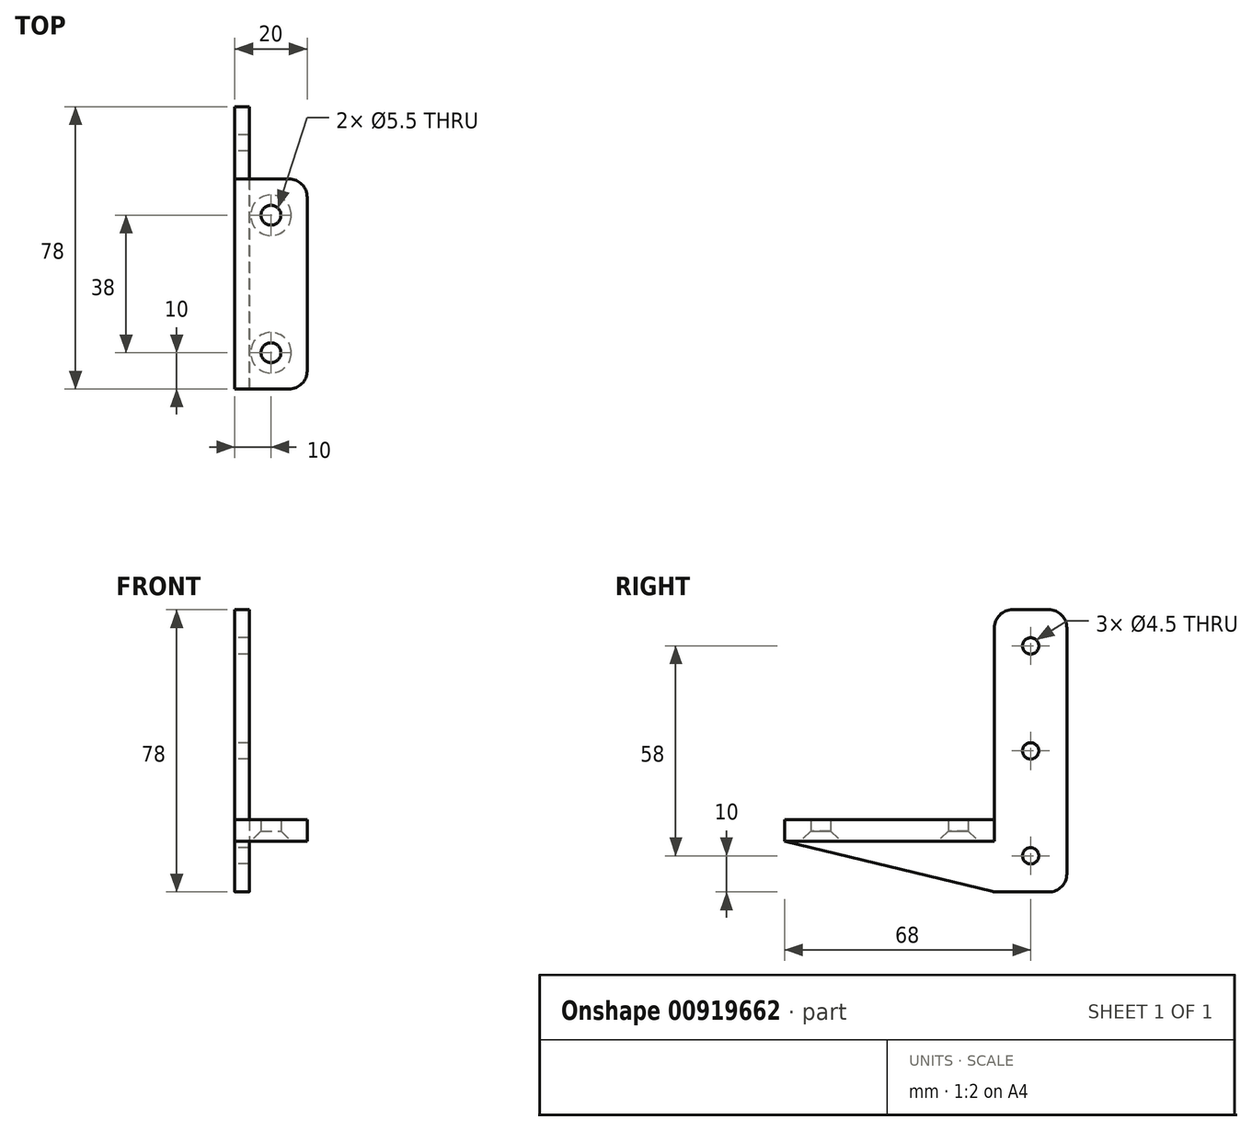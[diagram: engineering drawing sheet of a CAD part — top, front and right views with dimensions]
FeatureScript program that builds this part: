
annotation { "Feature Type Name" : "Feature", "Feature Type Description" : "" }
export const myFeature = defineFeature(function(context is Context, id is Id, definition is map)
    precondition{}
    {
        {
            var Q0;
            Q0=qCreatedBy(makeId("Right.planeOp"),FACE);
            var sketch = newSketch(context, id + "F0", { "sketchPlane" : qUnion([Q0])});
            skLineSegment(sketch, "E0", {"start": v(-29, 0) * mm, "end": v(29, 0) * mm});
            skLineSegment(sketch, "E1", {"start": v(29, -6) * mm, "end": v(-29, -6) * mm});
            skLineSegment(sketch, "E2", {"start": v(-29, 0) * mm, "end": v(-29, -6) * mm});
            skLineSegment(sketch, "E3", {"start": v(29, 0) * mm, "end": v(29, -6) * mm});
            skSolve(sketch);
        }
        {
            var Q0;
            Q0=qCreatedBy(makeId("Right.planeOp"),FACE);
            var sketch = newSketch(context, id + "F1", { "sketchPlane" : qUnion([Q0])});
            skLineSegment(sketch, "E4", {"start": v(-29, -6) * mm, "end": v(29, -20) * mm});
            skLineSegment(sketch, "E5", {"start": v(29, -20) * mm, "end": v(49, -20) * mm});
            skLineSegment(sketch, "E6", {"start": v(49, -20) * mm, "end": v(49, 58) * mm});
            skLineSegment(sketch, "E7", {"start": v(49, 58) * mm, "end": v(29, 58) * mm});
            skLineSegment(sketch, "E8", {"start": v(29, 58) * mm, "end": v(29, 0) * mm});
            skLineSegment(sketch, "E9", {"start": v(29, 0) * mm, "end": v(-29, 0) * mm});
            skLineSegment(sketch, "E10", {"start": v(-29, 0) * mm, "end": v(-29, -6) * mm});
            skLineSegment(sketch, "E11", {"start": v(39, 48) * mm, "end": v(39, -10) * mm, "construction": true});
            skPoint(sketch, "E12", {"position": v(39, 19) * mm});
            skSolve(sketch);
        }
        {
            var Q0;
            Q0 = qSketchRegion(id + "F0", true);
            extrude(context, id + "F2", {"entities" : qUnion([Q0]), "depth" : 20 * mm, "offsetDistance" : 25 * mm});
        }
        {
            var Q0;
            Q0 = qSketchRegion(id + "F1", true);
            extrude(context, id + "F3", {"entities" : qUnion([Q0]), "operationType" : NewBodyOperationType.ADD, "depth" : 4 * mm, "offsetDistance" : 25 * mm});
        }
        {
            var Q0;
            Q0=makeQuery(id+"F2.opExtrude","SWEPT_FACE",FACE,{"disambiguationData":[OSD([sQuery(id+"F0.wireOp",EDGE,"E1")])]});
            var sketch = newSketch(context, id + "F4", { "sketchPlane" : qUnion([Q0])});
            skLineSegment(sketch, "E13", {"start": v(10, 19) * mm, "end": v(10, -19) * mm, "construction": true});
            skSolve(sketch);
        }
        {
            var Q0;
            Q0=sQuery(id+"F4.wireOp",VERTEX,"E13.end");
            var Q1;
            Q1=sQuery(id+"F4.wireOp",VERTEX,"E13.start");
            var Q2;
            Q2=makeQuery(id+"F2.opExtrude","SWEPT_BODY",BODY,{"disambiguationData":[OSD([sQuery(id+"F0.wireOp",EDGE,"E0"),sQuery(id+"F0.wireOp",EDGE,"E1"),sQuery(id+"F0.wireOp",EDGE,"E2"),sQuery(id+"F0.wireOp",EDGE,"E3")])]});
            hole(context, id + "F5", {"style" : HoleStyle.C_SINK, "endStyle" : HoleEndStyle.BLIND, "standardTappedOrClearance" : lookupTablePath({ "fit" : "Normal", "standard" : "ISO", "size" : "M5", "type" : "Clearance" }), "standardBlindInLast" : lookupTablePath({ "fit" : "Normal", "standard" : "ISO", "engagement" : "75%", "pitch" : "0.8 mm", "size" : "M5", "type" : "Clearance & tapped" }), "holeDiameter" : 5.5 * mm, "cSinkDiameter" : 11.2 * mm, "cSinkAngle" : 90 * degree, "majorDiameter" : 5 * mm, "holeDepth" : 15 * mm, "isTappedThrough" : true, "tappedDepth" : 12 * mm, "tapClearance" : 3, "locations" : qUnion([Q0, Q1]), "scope" : qUnion([Q2])});
        }
        {
            var Q0;
            Q0=makeQuery(id+"F2.opExtrude","CAP_EDGE",EDGE,{"disambiguationData":[OSD([sQuery(id+"F0.wireOp",EDGE,"E2")])],"isStart":false});
            var Q1;
            Q1=makeQuery(id+"F2.opExtrude","CAP_EDGE",EDGE,{"disambiguationData":[OSD([sQuery(id+"F0.wireOp",EDGE,"E3")])],"isStart":false});
            var Q2;
            Q2=makeQuery(id+"F3.opExtrude","SWEPT_EDGE",EDGE,{"disambiguationData":[OSD([sQuery(id+"F1.wireOp",EDGE,"E7"),sQuery(id+"F1.wireOp",EDGE,"E8")])]});
            var Q3;
            Q3=makeQuery(id+"F3.opExtrude","SWEPT_EDGE",EDGE,{"disambiguationData":[OSD([sQuery(id+"F1.wireOp",EDGE,"E6"),sQuery(id+"F1.wireOp",EDGE,"E7")])]});
            var Q4;
            Q4=makeQuery(id+"F3.opExtrude","SWEPT_EDGE",EDGE,{"disambiguationData":[OSD([sQuery(id+"F1.wireOp",EDGE,"E5"),sQuery(id+"F1.wireOp",EDGE,"E6")])]});
            var Q5;
            Q5=makeQuery(id+"F3.opExtrude","SWEPT_EDGE",EDGE,{"disambiguationData":[OSD([sQuery(id+"F1.wireOp",EDGE,"E4"),sQuery(id+"F1.wireOp",EDGE,"E5")])]});
            fillet(context, id + "F6", {"entities" : qUnion([Q0, Q1, Q2, Q3, Q4, Q5]), "radius" : 5 * mm, "tangentPropagation" : true, "allowEdgeOverflow" : false});
        }
        {
            var Q0;
            Q0=sQuery(id+"F1.wireOp",VERTEX,"E11.start");
            var Q1;
            Q1=sQuery(id+"F1.wireOp",VERTEX,"E12");
            var Q2;
            Q2=sQuery(id+"F1.wireOp",VERTEX,"E11.end");
            var Q3;
            Q3=makeQuery(id+"F2.opExtrude","SWEPT_BODY",BODY,{"disambiguationData":[OSD([sQuery(id+"F0.wireOp",EDGE,"E0"),sQuery(id+"F0.wireOp",EDGE,"E1"),sQuery(id+"F0.wireOp",EDGE,"E2"),sQuery(id+"F0.wireOp",EDGE,"E3")])]});
            hole(context, id + "F7", {"style" : HoleStyle.SIMPLE, "endStyle" : HoleEndStyle.BLIND, "oppositeDirection" : true, "standardTappedOrClearance" : lookupTablePath({ "fit" : "Normal", "standard" : "ISO", "size" : "M4", "type" : "Clearance" }), "standardBlindInLast" : lookupTablePath({ "fit" : "Normal", "standard" : "ISO", "engagement" : "75%", "pitch" : "0.7 mm", "size" : "M4", "type" : "Clearance & tapped" }), "holeDiameter" : 4.5 * mm, "majorDiameter" : 5 * mm, "holeDepth" : 15 * mm, "isTappedThrough" : true, "tappedDepth" : 12 * mm, "tapClearance" : 3, "locations" : qUnion([Q0, Q1, Q2]), "scope" : qUnion([Q3])});
        }
    });
